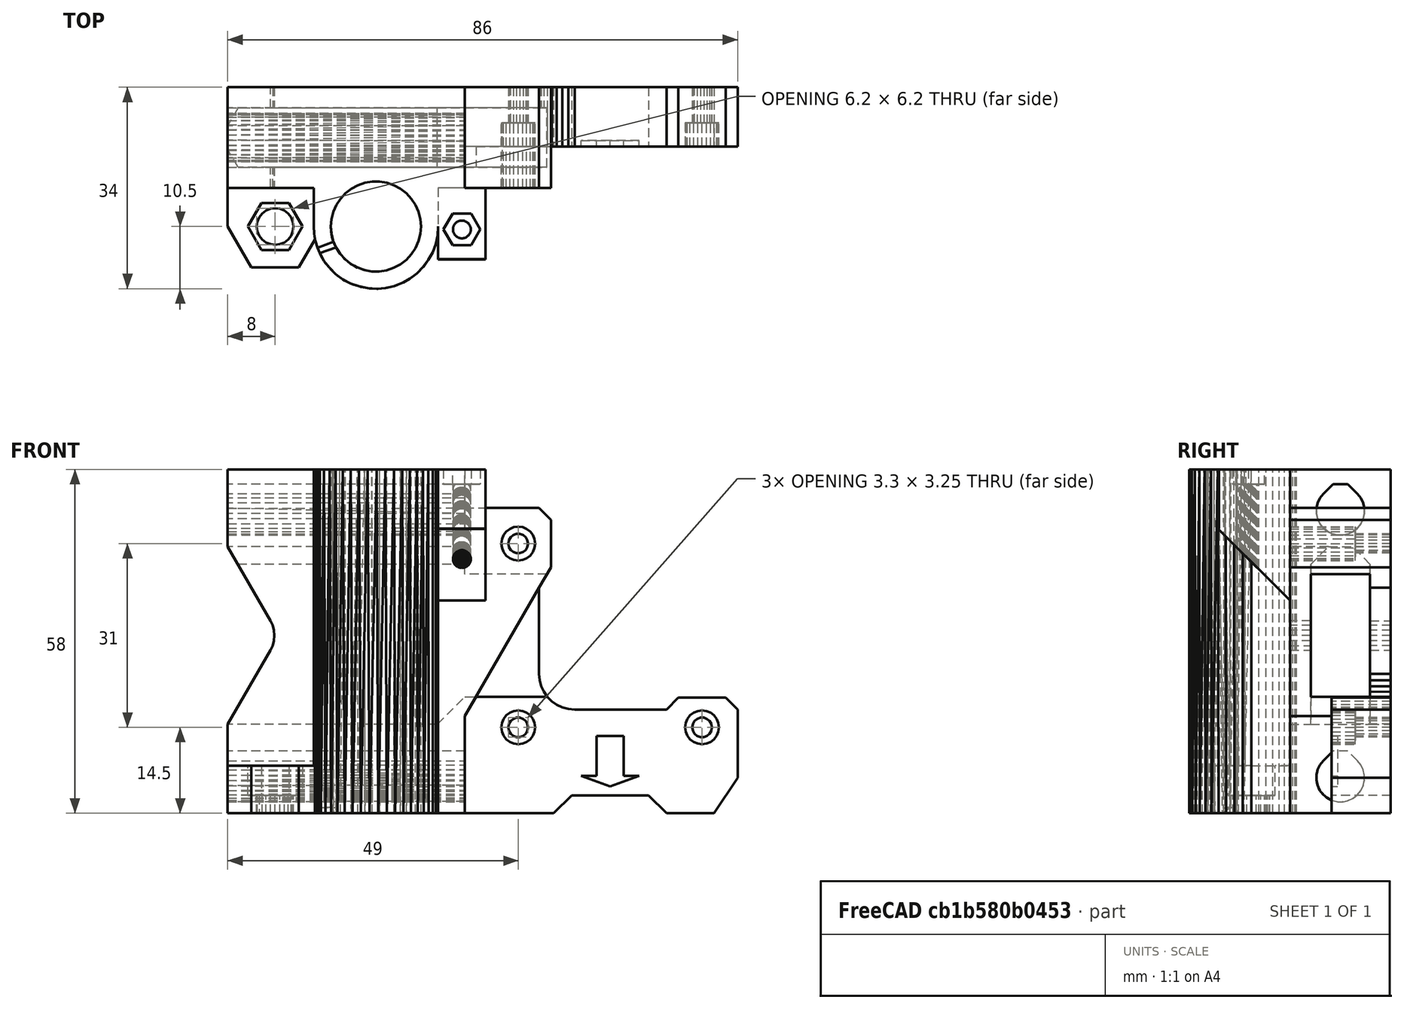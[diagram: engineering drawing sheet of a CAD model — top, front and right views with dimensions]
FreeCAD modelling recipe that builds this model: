
FCSTD DOCUMENT  (FreeCAD 0.15R4671 (Git))
Label: Prueba
License: All rights reserved
LicenseURL: http://es.wikipedia.org/wiki/Todos_los_derechos_reservados
objects: Part::Feature×3, Mesh::Feature×1, Sketcher::SketchObject×1, PartDesign::Pocket×1
note: 6 computed .brp shape members not serialized (recipe doc carries the construction recipe); baked Part::Feature solids carry a one-line shape summary decoded from their .brp

FEATURE [Mesh::Feature] EjeX_izquierda
FEATURE [Part::Feature] EjeX_izquierda001
  shape: bbox 86 x 34 x 58 mm, 1804 faces, 0 solids (baked)
FEATURE [Part::Feature] EjeX_izquierda001_solid  label="EjeX_izquierda001 (Solid)"
  shape: bbox 86 x 34 x 58 mm, 1804 faces (baked)
FEATURE [Part::Feature] EjeX_izquierda001_solid001  label="EjeX_izquierda001 (Solid)001"
  shape: bbox 86 x 34 x 58 mm, 652 faces (baked)
FEATURE [Sketcher::SketchObject] Sketch
  ExternalGeometry = -> [EjeX_izquierda001_solid001]
  Placement = pos=(0,0,0) rot=(1,0,0;1.5708rad)
  Support = -> EjeX_izquierda001_solid001 [Face288]
  sketch-geometry (9):
    g0: LineSegment StartX=22.2072 StartY=13.0422 StartZ=0 EndX=26.7928 EndY=13.0422 EndZ=0
    g1: LineSegment StartX=26.7928 StartY=13.0422 StartZ=0 EndX=26.7928 EndY=6.32709 EndZ=0
    g2: LineSegment StartX=26.7928 StartY=6.32709 StartZ=0 EndX=29.4108 EndY=6.32709 EndZ=0
    g3: LineSegment StartX=29.4108 StartY=6.32709 StartZ=0 EndX=24.5 EndY=4.53136 EndZ=0
    g4: LineSegment StartX=24.5 StartY=4.53136 StartZ=0 EndX=19.5892 EndY=6.32709 EndZ=0
    g5: LineSegment StartX=19.5892 StartY=6.32709 StartZ=0 EndX=22.2072 EndY=6.32709 EndZ=0
    g6: LineSegment StartX=22.2072 StartY=6.32709 StartZ=0 EndX=22.2072 EndY=13.0422 EndZ=0
    g7: LineSegment [constr] StartX=18 StartY=3 StartZ=0 EndX=24.5 EndY=4.53136 EndZ=0
    g8: LineSegment [constr] StartX=24.5 StartY=4.53136 StartZ=0 EndX=31 EndY=3 EndZ=0
  constraints (20):
    c: Coincident(g0,g6)
    c: Coincident(g0,g1)
    c: Coincident(g1,g2)
    c: Coincident(g2,g3)
    c: Coincident(g4,g5)
    c: Coincident(g5,g6)
    c: Equal(g5,g2)
    c: Horizontal(g2)
    c: Horizontal(g5)
    c: Horizontal(g0)
    c: Vertical(g6)
    c: Vertical(g1)
    c: Equal(g6,g1)
    c: Coincident(g4,g3)
    c: Equal(g4,g3)
    c: Coincident(g7,g-3)
    c: Coincident(g7,g3)
    c: Coincident(g8,g3)
    c: Coincident(g8,g-3)
    c: Equal(g8,g7)
FEATURE [PartDesign::Pocket] Pocket
  Length = 1
  Sketch = -> Sketch
  Type = 0
